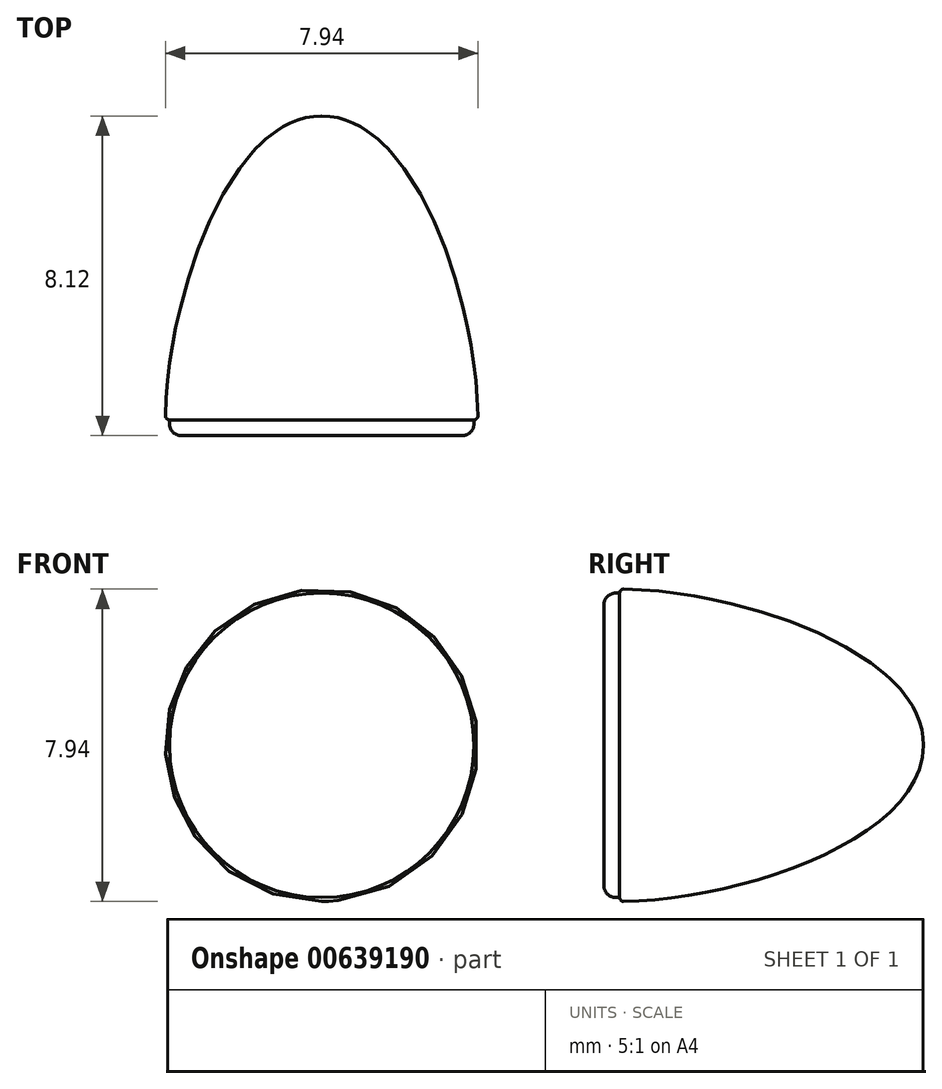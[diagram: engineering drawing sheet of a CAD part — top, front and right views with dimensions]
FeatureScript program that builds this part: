
annotation { "Feature Type Name" : "Feature", "Feature Type Description" : "" }
export const myFeature = defineFeature(function(context is Context, id is Id, definition is map)
    precondition{}
    {
        {
            var Q0;
            Q0=qCreatedBy(makeId("Right.planeOp"),FACE);
            var sketch = newSketch(context, id + "F0", { "sketchPlane" : qUnion([Q0])});
            skLineSegment(sketch, "E0", {"start": v(-7.46, 0) * mm, "end": v(7.72, 0) * mm, "construction": true});
            skLineSegment(sketch, "E1", {"start": v(0, 0) * mm, "end": v(0, -3.97) * mm, "construction": true});
            skPoint(sketch, "E2.orphan", {"position": v(0, 5.07) * mm});
            skFitSpline(sketch, "E3", {"points": [v(0, -3.97) * mm, v(7.72, 0) * mm], "startDerivative": vector(8.68, 0) * mm, "endDerivative": vector(0, 7.29) * mm});
            skLineSegment(sketch, "E4", {"start": v(7.72, 0) * mm, "end": v(7.72, 4.51) * mm, "construction": true});
            skLineSegment(sketch, "E5", {"start": v(0, -3.97) * mm, "end": v(-9.45, -3.97) * mm, "construction": true});
            skLineSegment(sketch, "E6", {"start": v(0, -3.97) * mm, "end": v(0, -3.87) * mm});
            skLineSegment(sketch, "E7", {"start": v(0, -3.87) * mm, "end": v(-0.4, -3.87) * mm});
            skLineSegment(sketch, "E8", {"start": v(-0.4, -3.87) * mm, "end": v(-0.4, 0) * mm});
            skLineSegment(sketch, "E9", {"start": v(-0.4, 0) * mm, "end": v(7.72, 0) * mm});
            skSolve(sketch);
        }
        {
            var Q0;
            Q0=makeQuery(id+"F0.imprint","IMPRINT",FACE,{"disambiguationData":[TD([[makeQuery(id+"F0.imprint","IMPRINT",EDGE,{"derivedFrom":sQuery(id+"F0.wireOp",EDGE,"E3")}),1.0]])]});
            var Q1;
            Q1=sQuery(id+"F0.wireOp",EDGE,"E0");
            revolve(context, id + "F1", {"entities" : qUnion([Q0]), "axis" : qUnion([Q1]), "revolveType" : RevolveType.FULL});
        }
        {
            var Q0;
            Q0=makeQuery(id+"F1.opRevolve","SWEPT_EDGE",EDGE,{"disambiguationData":[OSD([sQuery(id+"F0.wireOp",EDGE,"E7"),sQuery(id+"F0.wireOp",EDGE,"E8")])]});
            fillet(context, id + "F2", {"entities" : qUnion([Q0]), "radius" : 0.3 * mm, "tangentPropagation" : true, "allowEdgeOverflow" : false});
        }
        {
            var Q0;
            Q0=makeQuery(id+"F1.opRevolve","SWEPT_EDGE",EDGE,{"disambiguationData":[OSD([sQuery(id+"F0.wireOp",EDGE,"E3"),sQuery(id+"F0.wireOp",EDGE,"E6")])]});
            fillet(context, id + "F3", {"entities" : qUnion([Q0]), "radius" : 0.1 * mm, "tangentPropagation" : true, "allowEdgeOverflow" : false});
        }
    });
